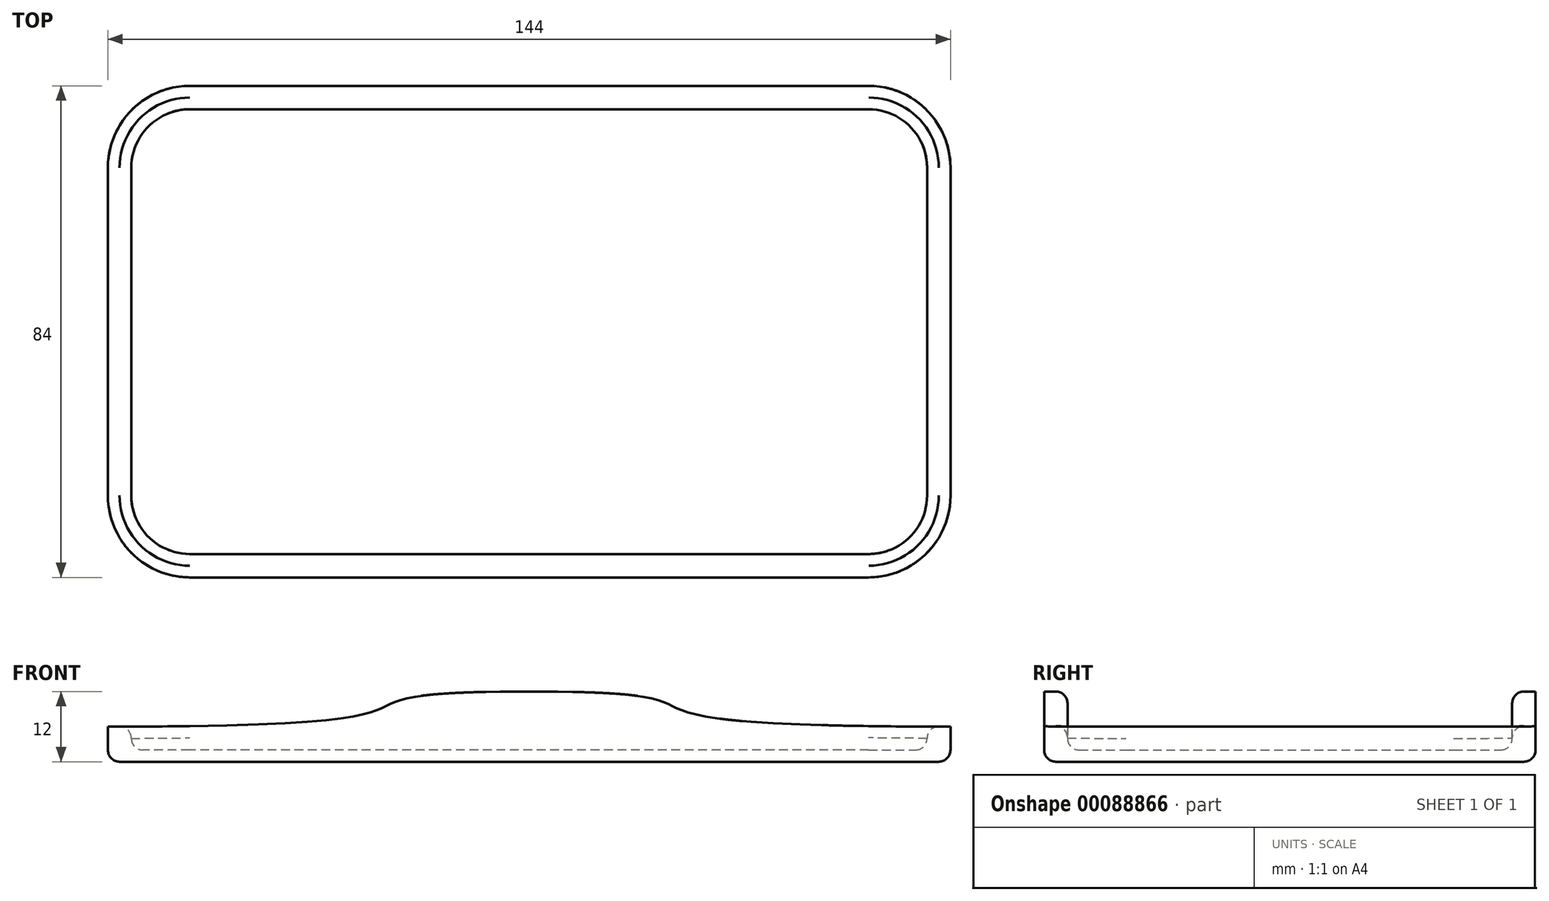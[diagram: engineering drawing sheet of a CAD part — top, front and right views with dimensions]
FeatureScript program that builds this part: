
annotation { "Feature Type Name" : "Feature", "Feature Type Description" : "" }
export const myFeature = defineFeature(function(context is Context, id is Id, definition is map)
    precondition{}
    {
        {
            var Q0;
            Q0=qCreatedBy(makeId("Top.planeOp"),FACE);
            var sketch = newSketch(context, id + "F0", { "sketchPlane" : qUnion([Q0])});
            skLineSegment(sketch, "E0.bottom", {"start": v(58, -38) * mm, "end": v(-58, -38) * mm});
            skLineSegment(sketch, "E0.top", {"start": v(58, 38) * mm, "end": v(-58, 38) * mm});
            skLineSegment(sketch, "E0.left", {"start": v(68, -28) * mm, "end": v(68, 28) * mm});
            skLineSegment(sketch, "E0.right", {"start": v(-68, -28) * mm, "end": v(-68, 28) * mm});
            skPoint(sketch, "E0.middle", {"position": v(0, 0) * mm});
            skPoint(sketch, "E1.visualSharp", {"position": v(-68, 38) * mm});
            skArc(sketch, "E1.filletArc", {"start": v(-58, 38) * mm, "mid": v(-65.07, 35.07) * mm, "end": v(-68, 28) * mm});
            skPoint(sketch, "E2.visualSharp", {"position": v(68, 38) * mm});
            skArc(sketch, "E2.filletArc", {"start": v(68, 28) * mm, "mid": v(65.07, 35.07) * mm, "end": v(58, 38) * mm});
            skPoint(sketch, "E3.visualSharp", {"position": v(68, -38) * mm});
            skArc(sketch, "E3.filletArc", {"start": v(58, -38) * mm, "mid": v(65.07, -35.07) * mm, "end": v(68, -28) * mm});
            skPoint(sketch, "E4.visualSharp", {"position": v(-68, -38) * mm});
            skArc(sketch, "E4.filletArc", {"start": v(-68, -28) * mm, "mid": v(-65.07, -35.07) * mm, "end": v(-58, -38) * mm});
            skLineSegment(sketch, "E5.0", {"start": v(58, 42) * mm, "end": v(-58, 42) * mm});
            skArc(sketch, "E5.1", {"start": v(72, 28) * mm, "mid": v(67.9, 37.9) * mm, "end": v(58, 42) * mm});
            skArc(sketch, "E5.2", {"start": v(-58, 42) * mm, "mid": v(-67.9, 37.9) * mm, "end": v(-72, 28) * mm});
            skLineSegment(sketch, "E5.3", {"start": v(72, -28) * mm, "end": v(72, 28) * mm});
            skLineSegment(sketch, "E5.4", {"start": v(-72, -28) * mm, "end": v(-72, 28) * mm});
            skArc(sketch, "E5.5", {"start": v(-72, -28) * mm, "mid": v(-67.9, -37.9) * mm, "end": v(-58, -42) * mm});
            skLineSegment(sketch, "E5.6", {"start": v(58, -42) * mm, "end": v(-58, -42) * mm});
            skArc(sketch, "E5.7", {"start": v(58, -42) * mm, "mid": v(67.9, -37.9) * mm, "end": v(72, -28) * mm});
            skSolve(sketch);
        }
        {
            var Q0;
            Q0=makeQuery(id+"F0.imprint","IMPRINT",FACE,{"disambiguationData":[TD([[makeQuery(id+"F0.imprint","IMPRINT",EDGE,{"derivedFrom":sQuery(id+"F0.wireOp",EDGE,"E0.top")}),1.0]])]});
            extrude(context, id + "F1", {"entities" : qUnion([Q0]), "depth" : 2 * mm});
        }
        {
            var Q0;
            Q0=makeQuery(id+"F0.imprint","IMPRINT",FACE,{"disambiguationData":[TD([[makeQuery(id+"F0.imprint","IMPRINT",EDGE,{"derivedFrom":sQuery(id+"F0.wireOp",EDGE,"E0.top")}),-1.0]])]});
            extrude(context, id + "F2", {"entities" : qUnion([Q0]), "operationType" : NewBodyOperationType.ADD, "depth" : 12 * mm});
        }
        {
            var Q0;
            Q0=qCreatedBy(makeId("Front.planeOp"),FACE);
            var sketch = newSketch(context, id + "F3", { "sketchPlane" : qUnion([Q0])});
            skLineSegment(sketch, "E6.0", {"start": v(72, 0) * mm, "end": v(-72, 0) * mm});
            skLineSegment(sketch, "E6.1", {"start": v(72, 12) * mm, "end": v(-72, 12) * mm});
            skLineSegment(sketch, "E7.0", {"start": v(-72, 12) * mm, "end": v(-72, 0) * mm});
            skLineSegment(sketch, "E8.0", {"start": v(72, 12) * mm, "end": v(72, 0) * mm});
            skFitSpline(sketch, "E9", {"points": [v(-72, 6) * mm, v(0, 12) * mm], "startDerivative": vector(216, 0) * mm, "endDerivative": vector(132.6, 0) * mm});
            skLineSegment(sketch, "E10", {"start": v(0, 12) * mm, "end": v(0, 0) * mm, "construction": true});
            skFitSpline(sketch, "E11.MirrorCS", {"points": [v(72, 6) * mm, v(0, 12) * mm], "startDerivative": vector(-216, 0) * mm, "endDerivative": vector(-132.6, 0) * mm});
            skPoint(sketch, "E12.orphan", {"position": v(-58, 0) * mm});
            skPoint(sketch, "E13.orphan", {"position": v(-58, 12) * mm});
            skPoint(sketch, "E14.orphan", {"position": v(58, 0) * mm});
            skPoint(sketch, "E15.orphan", {"position": v(58, 12) * mm});
            skSolve(sketch);
        }
        {
            var Q0;
            {var subQ2=sQuery(id+"F3.wireOp",EDGE,"E6.0");Q0=makeQuery(id+"F3.imprint","IMPRINT",FACE,{"disambiguationData":[TD([[makeQuery(id+"F3.imprint","IMPRINT",EDGE,{"derivedFrom":subQ2}),-1.0]])]});}
            extrude(context, id + "F4", {"entities" : qUnion([Q0]), "operationType" : NewBodyOperationType.INTERSECT, "endBound" : BoundingType.SYMMETRIC, "depth" : 99 * mm});
        }
        {
            var Q0;
            Q0=makeQuery(id+"F2.opExtrude","SWEPT_FACE",FACE,{"disambiguationData":[OSD([sQuery(id+"F0.wireOp",EDGE,"E2.filletArc")])]});
            var Q1;
            Q1=makeQuery(id+"F1.opExtrude","CAP_EDGE",EDGE,{"disambiguationData":[OSD([sQuery(id+"F0.wireOp",EDGE,"E2.filletArc")])],"isStart":false});
            var Q2;
            Q2=makeQuery(id+"F4.boolean.opBoolean","INTERSECT",EDGE,{"derivedFrom":[makeQuery(id+"F2.opExtrude","SWEPT_FACE",FACE,{"disambiguationData":[OSD([sQuery(id+"F0.wireOp",EDGE,"E2.filletArc")])]}),makeQuery(id+"F4.boolean.toolComplement.opBoolean","COPY",FACE,{"derivedFrom":makeQuery(id+"F4.opExtrude","SWEPT_FACE",FACE,{"disambiguationData":[OSD([sQuery(id+"F3.wireOp",EDGE,"E11.MirrorCS")])]})})]});
            var Q3;
            Q3=makeQuery(id+"F4.boolean.opBoolean","INTERSECT",EDGE,{"derivedFrom":[makeQuery(id+"F2.opExtrude","SWEPT_FACE",FACE,{"disambiguationData":[OSD([sQuery(id+"F0.wireOp",EDGE,"E5.1")])]}),makeQuery(id+"F4.boolean.toolComplement.opBoolean","COPY",FACE,{"derivedFrom":makeQuery(id+"F4.opExtrude","SWEPT_FACE",FACE,{"disambiguationData":[OSD([sQuery(id+"F3.wireOp",EDGE,"E11.MirrorCS")])]})})]});
            var Q4;
            Q4=makeQuery(id+"F4.boolean.opBoolean","INTERSECT",EDGE,{"derivedFrom":[makeQuery(id+"F2.opExtrude","SWEPT_FACE",FACE,{"disambiguationData":[OSD([sQuery(id+"F0.wireOp",EDGE,"E5.7")])]}),makeQuery(id+"F4.boolean.toolComplement.opBoolean","COPY",FACE,{"derivedFrom":makeQuery(id+"F4.opExtrude","SWEPT_FACE",FACE,{"disambiguationData":[OSD([sQuery(id+"F3.wireOp",EDGE,"E11.MirrorCS")])]})})]});
            var Q5;
            Q5=makeQuery(id+"F2.opExtrude","CAP_EDGE",EDGE,{"disambiguationData":[OSD([sQuery(id+"F0.wireOp",EDGE,"E5.7")])],"isStart":true});
            var Q6;
            Q6=makeQuery(id+"F4.boolean.opBoolean","INTERSECT",EDGE,{"derivedFrom":[makeQuery(id+"F2.opExtrude","SWEPT_FACE",FACE,{"disambiguationData":[OSD([sQuery(id+"F0.wireOp",EDGE,"E3.filletArc")])]}),makeQuery(id+"F4.boolean.toolComplement.opBoolean","COPY",FACE,{"derivedFrom":makeQuery(id+"F4.opExtrude","SWEPT_FACE",FACE,{"disambiguationData":[OSD([sQuery(id+"F3.wireOp",EDGE,"E11.MirrorCS")])]})})]});
            var Q7;
            Q7=makeQuery(id+"F2.opExtrude","CAP_EDGE",EDGE,{"disambiguationData":[OSD([sQuery(id+"F0.wireOp",EDGE,"E5.5")])],"isStart":true});
            var Q8;
            Q8=makeQuery(id+"F4.boolean.opBoolean","INTERSECT",EDGE,{"derivedFrom":[makeQuery(id+"F2.opExtrude","SWEPT_FACE",FACE,{"disambiguationData":[OSD([sQuery(id+"F0.wireOp",EDGE,"E5.5")])]}),makeQuery(id+"F4.boolean.toolComplement.opBoolean","COPY",FACE,{"derivedFrom":makeQuery(id+"F4.opExtrude","SWEPT_FACE",FACE,{"disambiguationData":[OSD([sQuery(id+"F3.wireOp",EDGE,"E9")])]})})]});
            var Q9;
            Q9=makeQuery(id+"F4.boolean.opBoolean","INTERSECT",EDGE,{"derivedFrom":[makeQuery(id+"F2.opExtrude","SWEPT_FACE",FACE,{"disambiguationData":[OSD([sQuery(id+"F0.wireOp",EDGE,"E4.filletArc")])]}),makeQuery(id+"F4.boolean.toolComplement.opBoolean","COPY",FACE,{"derivedFrom":makeQuery(id+"F4.opExtrude","SWEPT_FACE",FACE,{"disambiguationData":[OSD([sQuery(id+"F3.wireOp",EDGE,"E9")])]})})]});
            var Q10;
            Q10=makeQuery(id+"F1.opExtrude","CAP_EDGE",EDGE,{"disambiguationData":[OSD([sQuery(id+"F0.wireOp",EDGE,"E1.filletArc")])],"isStart":false});
            var Q11;
            Q11=makeQuery(id+"F4.boolean.opBoolean","INTERSECT",EDGE,{"derivedFrom":[makeQuery(id+"F2.opExtrude","SWEPT_FACE",FACE,{"disambiguationData":[OSD([sQuery(id+"F0.wireOp",EDGE,"E1.filletArc")])]}),makeQuery(id+"F4.boolean.toolComplement.opBoolean","COPY",FACE,{"derivedFrom":makeQuery(id+"F4.opExtrude","SWEPT_FACE",FACE,{"disambiguationData":[OSD([sQuery(id+"F3.wireOp",EDGE,"E9")])]})})]});
            var Q12;
            Q12=makeQuery(id+"F4.boolean.opBoolean","INTERSECT",EDGE,{"derivedFrom":[makeQuery(id+"F2.opExtrude","SWEPT_FACE",FACE,{"disambiguationData":[OSD([sQuery(id+"F0.wireOp",EDGE,"E5.2")])]}),makeQuery(id+"F4.boolean.toolComplement.opBoolean","COPY",FACE,{"derivedFrom":makeQuery(id+"F4.opExtrude","SWEPT_FACE",FACE,{"disambiguationData":[OSD([sQuery(id+"F3.wireOp",EDGE,"E9")])]})})]});
            fillet(context, id + "F5", {"entities" : qUnion([Q0, Q1, Q2, Q3, Q4, Q5, Q6, Q7, Q8, Q9, Q10, Q11, Q12]), "radius" : 2 * mm, "tangentPropagation" : true, "allowEdgeOverflow" : false});
        }
    });
